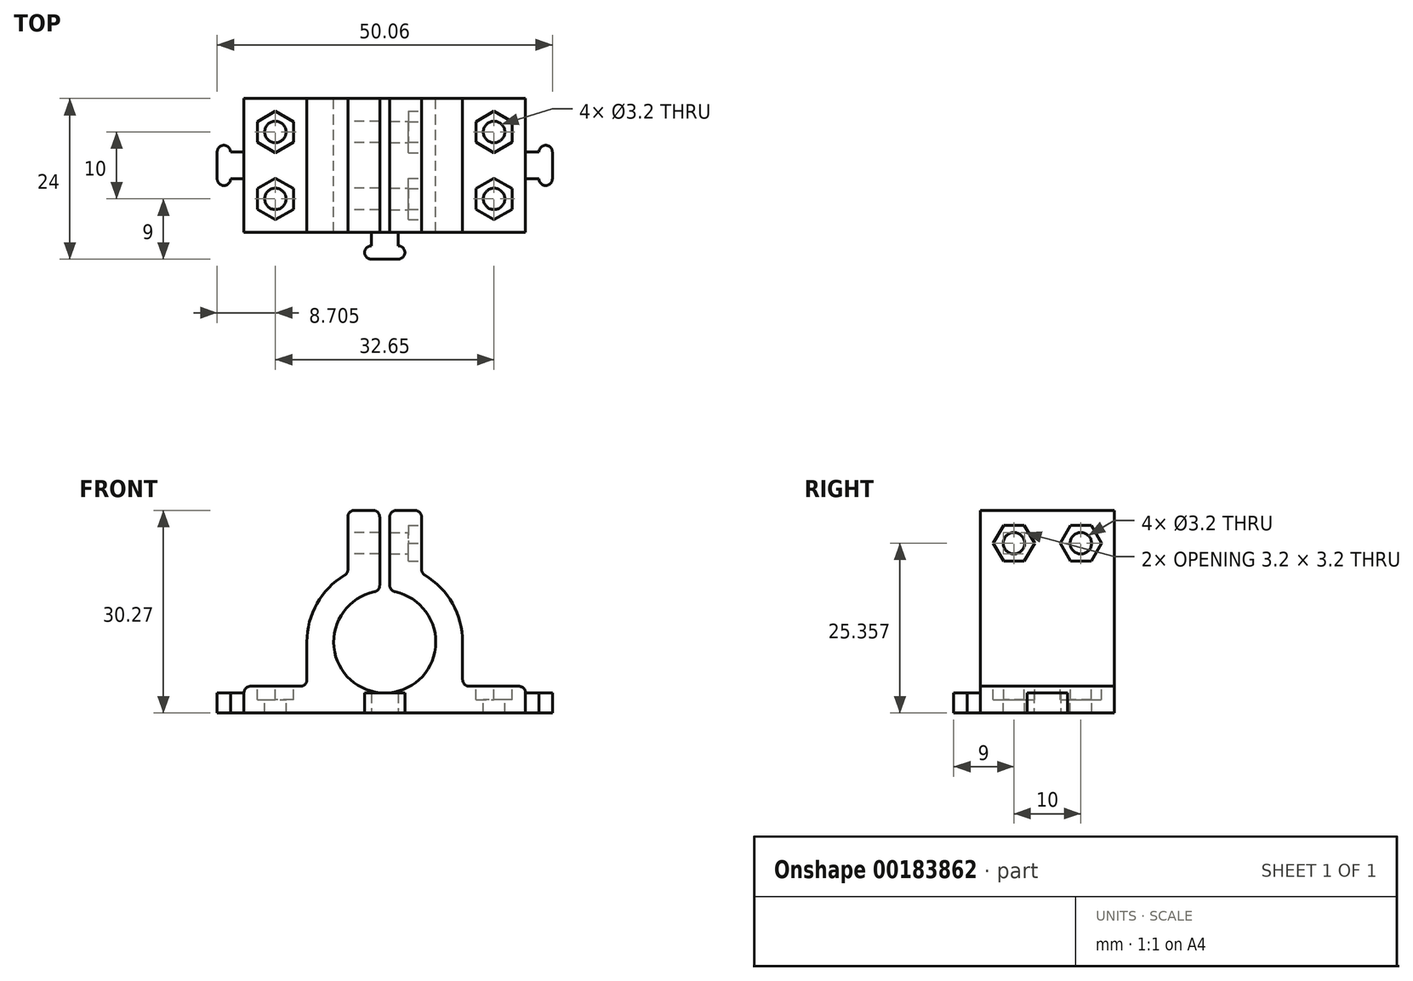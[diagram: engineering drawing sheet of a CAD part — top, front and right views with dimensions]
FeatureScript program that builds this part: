
annotation { "Feature Type Name" : "Feature", "Feature Type Description" : "" }
export const myFeature = defineFeature(function(context is Context, id is Id, definition is map)
    precondition{}
    {
        {
            assignVariable(context, id + "F0", {"name" : "hole_d_ideal", "anyValue" : 3});
        }
        {
            assignVariable(context, id + "F1", {"name" : "hole_d_pad", "anyValue" : 0.2});
        }
        {
            assignVariable(context, id + "F2", {"name" : "nut_h", "anyValue" : 2});
        }
        {
            assignVariable(context, id + "F3", {"name" : "hole_d", "anyValue" : getVariable(context, 'hole_d_ideal') + getVariable(context, 'hole_d_pad')});
        }
        {
            assignVariable(context, id + "F4", {"name" : "bear_l", "anyValue" : 24});
        }
        {
            assignVariable(context, id + "F5", {"name" : "base_l", "anyValue" : getVariable(context, 'bear_l') - 4});
        }
        {
            var Q0;
            Q0=qCreatedBy(makeId("Front.planeOp"),FACE);
            var sketch = newSketch(context, id + "F6", { "sketchPlane" : qUnion([Q0])});
            skLineSegment(sketch, "E0", {"start": v(0, 0) * mm, "end": v(21.03, 0) * mm});
            skLineSegment(sketch, "E1", {"start": v(21.03, 0) * mm, "end": v(21.03, 4) * mm});
            skLineSegment(sketch, "E2", {"start": v(21.03, 4) * mm, "end": v(11.62, 4) * mm});
            skLineSegment(sketch, "E3", {"start": v(11.62, 4) * mm, "end": v(11.62, 10.62) * mm});
            skArc(sketch, "E4", {"start": v(0, 3) * mm, "mid": v(7.62, 10.25) * mm, "end": v(0.75, 18.21) * mm});
            skLineSegment(sketch, "E5.top", {"start": v(0.75, 30.27) * mm, "end": v(5.5, 30.27) * mm});
            skLineSegment(sketch, "E5.right", {"start": v(5.5, 20.87) * mm, "end": v(5.5, 30.27) * mm});
            skLineSegment(sketch, "E6.trimOffspring", {"start": v(0, 3) * mm, "end": v(0, 0) * mm});
            skPoint(sketch, "E7", {"position": v(11.62, 10.62) * mm});
            skArc(sketch, "E8", {"start": v(11.62, 10.62) * mm, "mid": v(9.98, 16.6) * mm, "end": v(5.5, 20.87) * mm});
            skLineSegment(sketch, "E9", {"start": v(0.75, 18.21) * mm, "end": v(0.75, 30.27) * mm});
            skSolve(sketch);
        }
        {
            var Q0;
            Q0 = qSketchRegion(id + "F6", true);
            extrude(context, id + "F7", {"entities" : qUnion([Q0]), "endBound" : BoundingType.SYMMETRIC, "depth" : (getVariable(context, 'base_l')) * mm});
        }
        {
            var Q0;
            Q0=makeQuery(id+"F7.opExtrude","SWEPT_EDGE",EDGE,{"disambiguationData":[OSD([sQuery(id+"F6.wireOp",EDGE,"E4"),sQuery(id+"F6.wireOp",EDGE,"E9")])]});
            var Q1;
            Q1=makeQuery(id+"F7.opExtrude","SWEPT_EDGE",EDGE,{"disambiguationData":[OSD([sQuery(id+"F6.wireOp",EDGE,"E5.top"),sQuery(id+"F6.wireOp",EDGE,"E5.right")])]});
            var Q2;
            Q2=makeQuery(id+"F7.opExtrude","SWEPT_EDGE",EDGE,{"disambiguationData":[OSD([sQuery(id+"F6.wireOp",EDGE,"E5.top"),sQuery(id+"F6.wireOp",EDGE,"E5.right")])]});
            var Q3;
            Q3=makeQuery(id+"F7.opExtrude","SWEPT_EDGE",EDGE,{"disambiguationData":[OSD([sQuery(id+"F6.wireOp",EDGE,"E5.right"),sQuery(id+"F6.wireOp",EDGE,"E8")])]});
            var Q4;
            Q4=makeQuery(id+"F7.opExtrude","SWEPT_EDGE",EDGE,{"disambiguationData":[OSD([sQuery(id+"F6.wireOp",EDGE,"E2"),sQuery(id+"F6.wireOp",EDGE,"E3")])]});
            var Q5;
            Q5=makeQuery(id+"F7.opExtrude","SWEPT_EDGE",EDGE,{"disambiguationData":[OSD([sQuery(id+"F6.wireOp",EDGE,"E3"),sQuery(id+"F6.wireOp",EDGE,"E8")])]});
            var Q6;
            Q6=makeQuery(id+"F7.opExtrude","SWEPT_EDGE",EDGE,{"disambiguationData":[OSD([sQuery(id+"F6.wireOp",EDGE,"E2"),sQuery(id+"F6.wireOp",EDGE,"E3")])]});
            var Q7;
            Q7=makeQuery(id+"F7.opExtrude","SWEPT_EDGE",EDGE,{"disambiguationData":[OSD([sQuery(id+"F6.wireOp",EDGE,"E1"),sQuery(id+"F6.wireOp",EDGE,"E2")])]});
            var Q8;
            Q8=makeQuery(id+"F7.opExtrude","SWEPT_EDGE",EDGE,{"disambiguationData":[OSD([sQuery(id+"F6.wireOp",EDGE,"E5.top"),sQuery(id+"F6.wireOp",EDGE,"E9")])]});
            var Q9;
            Q9=makeQuery(id+"F7.opExtrude","SWEPT_EDGE",EDGE,{"disambiguationData":[OSD([sQuery(id+"F6.wireOp",EDGE,"E5.top"),sQuery(id+"F6.wireOp",EDGE,"E5.right")])]});
            fillet(context, id + "F8", {"entities" : qUnion([Q0, Q1, Q2, Q3, Q4, Q5, Q6, Q7, Q8, Q9]), "radius" : 1 * mm, "tangentPropagation" : true, "allowEdgeOverflow" : false});
        }
        {
            var Q0;
            Q0=makeQuery(id+"F7.opExtrude","SWEPT_FACE",FACE,{"disambiguationData":[OSD([sQuery(id+"F6.wireOp",EDGE,"E5.right")])]});
            var sketch = newSketch(context, id + "F9", { "sketchPlane" : qUnion([Q0])});
            skLineSegment(sketch, "E10", {"start": v(-10, 25.36) * mm, "end": v(0, 25.36) * mm, "construction": true});
            skLineSegment(sketch, "E11", {"start": v(0, 25.36) * mm, "end": v(10, 25.36) * mm, "construction": true});
            skPoint(sketch, "E12", {"position": v(-5, 25.36) * mm});
            skPoint(sketch, "E13", {"position": v(5, 25.36) * mm});
            skPoint(sketch, "E14", {"position": v(-10, 25.36) * mm});
            skCircle(sketch, "E15.cCircle", {"center": v(-5, 25.36) * mm, "radius": 3.1 * mm, "construction": true});
            skLineSegment(sketch, "E15.0", {"start": v(-3.45, 28.04) * mm, "end": v(-1.9, 25.36) * mm});
            skLineSegment(sketch, "E15.1", {"start": v(-1.9, 25.36) * mm, "end": v(-3.45, 22.67) * mm});
            skLineSegment(sketch, "E15.2", {"start": v(-3.45, 22.67) * mm, "end": v(-6.55, 22.67) * mm});
            skLineSegment(sketch, "E15.3", {"start": v(-6.55, 22.67) * mm, "end": v(-8.1, 25.36) * mm});
            skLineSegment(sketch, "E15.4", {"start": v(-8.1, 25.36) * mm, "end": v(-6.55, 28.04) * mm});
            skLineSegment(sketch, "E15.5", {"start": v(-6.55, 28.04) * mm, "end": v(-3.45, 28.04) * mm});
            skCircle(sketch, "E16.cCircle", {"center": v(5, 25.36) * mm, "radius": 3.1 * mm, "construction": true});
            skLineSegment(sketch, "E16.0", {"start": v(3.45, 28.04) * mm, "end": v(6.55, 28.04) * mm});
            skLineSegment(sketch, "E16.1", {"start": v(6.55, 28.04) * mm, "end": v(8.1, 25.36) * mm});
            skLineSegment(sketch, "E16.2", {"start": v(8.1, 25.36) * mm, "end": v(6.55, 22.67) * mm});
            skLineSegment(sketch, "E16.3", {"start": v(6.55, 22.67) * mm, "end": v(3.45, 22.67) * mm});
            skLineSegment(sketch, "E16.4", {"start": v(3.45, 22.67) * mm, "end": v(1.9, 25.36) * mm});
            skLineSegment(sketch, "E16.5", {"start": v(1.9, 25.36) * mm, "end": v(3.45, 28.04) * mm});
            skSolve(sketch);
        }
        {
            var Q0;
            Q0=sQuery(id+"F9.wireOp",VERTEX,"E12");
            var Q1;
            Q1=sQuery(id+"F9.wireOp",VERTEX,"E13");
            var Q2;
            Q2=makeQuery(id+"F7.opExtrude","SWEPT_BODY",BODY,{"disambiguationData":[OSD([sQuery(id+"F6.wireOp",EDGE,"E0"),sQuery(id+"F6.wireOp",EDGE,"E1"),sQuery(id+"F6.wireOp",EDGE,"E2"),sQuery(id+"F6.wireOp",EDGE,"E3"),sQuery(id+"F6.wireOp",EDGE,"HN3FgCps-Q0FI-6wMn-lYnE-is20jSelRbzD"),sQuery(id+"F6.wireOp",EDGE,"b23bd27e-2929-432b-ba1c-64cbd251a3970.MirrorCS"),sQuery(id+"F6.wireOp",EDGE,"2befd7d9-4525-4836-902e-ac56c651b7a10.MirrorCS"),sQuery(id+"F6.wireOp",EDGE,"45559492-88bf-4efa-95f0-e6e5f18770240.MirrorCS"),sQuery(id+"F6.wireOp",EDGE,"8ad17469-4e6f-47e4-abdb-9c6c75d0893b0.MirrorCS"),sQuery(id+"F6.wireOp",EDGE,"a78b3f0d-bb6c-460a-9a47-5c75e2336ab60.MirrorCS"),sQuery(id+"F6.wireOp",EDGE,"E4"),sQuery(id+"F6.wireOp",EDGE,"E5.top"),sQuery(id+"F6.wireOp",EDGE,"E5.right"),sQuery(id+"F6.wireOp",EDGE,"feef7f43-0b31-40ae-9d8b-5ec27f5b37380.MirrorCS"),sQuery(id+"F6.wireOp",EDGE,"c6b9ee4f-cf07-424e-834d-23f5c7f768820.MirrorCS")])]});
            hole(context, id + "F10", {"style" : HoleStyle.SIMPLE, "endStyle" : HoleEndStyle.THROUGH, "holeDiameter" : (getVariable(context, 'hole_d')) * mm, "locations" : qUnion([Q0, Q1]), "scope" : qUnion([Q2]), "isTappedThrough" : true});
        }
        {
            var Q0;
            Q0=makeQuery(id+"F7.opExtrude","SWEPT_FACE",FACE,{"disambiguationData":[OSD([sQuery(id+"F6.wireOp",EDGE,"E2")])]});
            var sketch = newSketch(context, id + "F11", { "sketchPlane" : qUnion([Q0])});
            skLineSegment(sketch, "E17", {"start": v(16.32, 10) * mm, "end": v(16.32, 0) * mm, "construction": true});
            skLineSegment(sketch, "E18", {"start": v(16.32, 0) * mm, "end": v(16.32, -10) * mm, "construction": true});
            skPoint(sketch, "E19", {"position": v(16.32, 5) * mm});
            skPoint(sketch, "E20", {"position": v(16.32, -5) * mm});
            skCircle(sketch, "E21.cCircle", {"center": v(16.32, 5) * mm, "radius": 3.1 * mm, "construction": true});
            skLineSegment(sketch, "E21.0", {"start": v(13.64, 6.55) * mm, "end": v(16.33, 8.1) * mm});
            skLineSegment(sketch, "E21.1", {"start": v(16.33, 8.1) * mm, "end": v(19, 6.55) * mm});
            skLineSegment(sketch, "E21.2", {"start": v(19, 6.55) * mm, "end": v(19, 3.45) * mm});
            skLineSegment(sketch, "E21.3", {"start": v(19, 3.45) * mm, "end": v(16.33, 1.9) * mm});
            skLineSegment(sketch, "E21.4", {"start": v(16.33, 1.9) * mm, "end": v(13.64, 3.45) * mm});
            skLineSegment(sketch, "E21.5", {"start": v(13.64, 3.45) * mm, "end": v(13.64, 6.55) * mm});
            skCircle(sketch, "E22.cCircle", {"center": v(16.32, -5) * mm, "radius": 3.1 * mm, "construction": true});
            skLineSegment(sketch, "E22.0", {"start": v(13.64, -3.45) * mm, "end": v(16.33, -1.9) * mm});
            skLineSegment(sketch, "E22.1", {"start": v(16.33, -1.9) * mm, "end": v(19, -3.45) * mm});
            skLineSegment(sketch, "E22.2", {"start": v(19, -3.45) * mm, "end": v(19, -6.55) * mm});
            skLineSegment(sketch, "E22.3", {"start": v(19, -6.55) * mm, "end": v(16.33, -8.1) * mm});
            skLineSegment(sketch, "E22.4", {"start": v(16.33, -8.1) * mm, "end": v(13.64, -6.55) * mm});
            skLineSegment(sketch, "E22.5", {"start": v(13.64, -6.55) * mm, "end": v(13.64, -3.45) * mm});
            skSolve(sketch);
        }
        {
            var Q0;
            Q0=sQuery(id+"F11.wireOp",VERTEX,"E19");
            var Q1;
            Q1=sQuery(id+"F11.wireOp",VERTEX,"E20");
            var Q2;
            Q2=makeQuery(id+"F7.opExtrude","SWEPT_BODY",BODY,{"disambiguationData":[OSD([sQuery(id+"F6.wireOp",EDGE,"E0"),sQuery(id+"F6.wireOp",EDGE,"E1"),sQuery(id+"F6.wireOp",EDGE,"E2"),sQuery(id+"F6.wireOp",EDGE,"E3"),sQuery(id+"F6.wireOp",EDGE,"HN3FgCps-Q0FI-6wMn-lYnE-is20jSelRbzD"),sQuery(id+"F6.wireOp",EDGE,"b23bd27e-2929-432b-ba1c-64cbd251a3970.MirrorCS"),sQuery(id+"F6.wireOp",EDGE,"2befd7d9-4525-4836-902e-ac56c651b7a10.MirrorCS"),sQuery(id+"F6.wireOp",EDGE,"45559492-88bf-4efa-95f0-e6e5f18770240.MirrorCS"),sQuery(id+"F6.wireOp",EDGE,"8ad17469-4e6f-47e4-abdb-9c6c75d0893b0.MirrorCS"),sQuery(id+"F6.wireOp",EDGE,"a78b3f0d-bb6c-460a-9a47-5c75e2336ab60.MirrorCS")])]});
            hole(context, id + "F12", {"style" : HoleStyle.SIMPLE, "endStyle" : HoleEndStyle.THROUGH, "holeDiameter" : (getVariable(context, 'hole_d')) * mm, "locations" : qUnion([Q0, Q1]), "scope" : qUnion([Q2]), "isTappedThrough" : true});
        }
        {
            var Q0;
            Q0=makeQuery(id+"F11.imprint","IMPRINT",FACE,{"disambiguationData":[TD([[makeQuery(id+"F11.imprint","IMPRINT",EDGE,{"derivedFrom":sQuery(id+"F11.wireOp",EDGE,"E21.0")}),-1.0]])]});
            var Q1;
            Q1=makeQuery(id+"F11.imprint","IMPRINT",FACE,{"disambiguationData":[TD([[makeQuery(id+"F11.imprint","IMPRINT",EDGE,{"derivedFrom":sQuery(id+"F11.wireOp",EDGE,"E22.0")}),-1.0]])]});
            extrude(context, id + "F13", {"entities" : qUnion([Q0, Q1]), "operationType" : NewBodyOperationType.REMOVE, "oppositeDirection" : true, "depth" : (getVariable(context, 'nut_h')) * mm});
        }
        {
            var Q0;
            Q0=makeQuery(id+"F7.opExtrude","SWEPT_FACE",FACE,{"disambiguationData":[OSD([sQuery(id+"F6.wireOp",EDGE,"E0")])]});
            var sketch = newSketch(context, id + "F14", { "sketchPlane" : qUnion([Q0])});
            skLineSegment(sketch, "E23", {"start": v(0, 10) * mm, "end": v(0, 14) * mm});
            skLineSegment(sketch, "E24", {"start": v(0, 14) * mm, "end": v(2, 14) * mm});
            skArc(sketch, "E25", {"start": v(2, 14) * mm, "mid": v(3, 13) * mm, "end": v(2, 12) * mm});
            skLineSegment(sketch, "E26", {"start": v(2, 12) * mm, "end": v(2, 10) * mm});
            skLineSegment(sketch, "E27", {"start": v(0, 10) * mm, "end": v(2, 10) * mm});
            skLineSegment(sketch, "E28", {"start": v(21.03, 0) * mm, "end": v(25.03, 0) * mm});
            skLineSegment(sketch, "E29", {"start": v(25.03, 0) * mm, "end": v(25.03, -2) * mm});
            skArc(sketch, "E30", {"start": v(25.03, -2) * mm, "mid": v(24.03, -3) * mm, "end": v(23.02, -2) * mm});
            skLineSegment(sketch, "E31", {"start": v(23.02, -2) * mm, "end": v(21.03, -2) * mm});
            skLineSegment(sketch, "E32", {"start": v(21.03, 0) * mm, "end": v(21.03, -2) * mm});
            skLineSegment(sketch, "E33.MirrorCS", {"start": v(23.02, 2) * mm, "end": v(21.03, 2) * mm});
            skLineSegment(sketch, "E34.MirrorCS", {"start": v(21.03, 0) * mm, "end": v(21.03, 2) * mm});
            skArc(sketch, "E35.MirrorCS", {"start": v(25.03, 2) * mm, "mid": v(24.03, 3) * mm, "end": v(23.02, 2) * mm});
            skLineSegment(sketch, "E36.MirrorCS", {"start": v(25.03, 0) * mm, "end": v(25.03, 2) * mm});
            skSolve(sketch);
        }
        {
            var Q0;
            Q0 = qSketchRegion(id + "F14", true);
            extrude(context, id + "F15", {"entities" : qUnion([Q0]), "operationType" : NewBodyOperationType.ADD, "oppositeDirection" : true, "depth" : 3 * mm});
        }
        {
            var Q0;
            Q0=makeQuery(id+"F7.opExtrude","SWEPT_BODY",BODY,{"disambiguationData":[OSD([sQuery(id+"F6.wireOp",EDGE,"E0"),sQuery(id+"F6.wireOp",EDGE,"E1"),sQuery(id+"F6.wireOp",EDGE,"E2"),sQuery(id+"F6.wireOp",EDGE,"E3"),sQuery(id+"F6.wireOp",EDGE,"E4"),sQuery(id+"F6.wireOp",EDGE,"E5.top"),sQuery(id+"F6.wireOp",EDGE,"E5.right"),sQuery(id+"F6.wireOp",EDGE,"E6.trimOffspring"),sQuery(id+"F6.wireOp",EDGE,"E8"),sQuery(id+"F6.wireOp",EDGE,"E9")])]});
            var Q1;
            Q1=qCreatedBy(makeId("Right.planeOp"),FACE);
            mirror(context, id + "F16", {"operationType" : NewBodyOperationType.ADD, "entities" : qUnion([Q0]), "mirrorPlane" : qUnion([Q1])});
        }
        {
            var Q0;
            Q0=makeQuery(id+"F9.imprint","IMPRINT",FACE,{"disambiguationData":[TD([[makeQuery(id+"F9.imprint","IMPRINT",EDGE,{"derivedFrom":sQuery(id+"F9.wireOp",EDGE,"E15.0")}),-1.0]])]});
            var Q1;
            Q1=makeQuery(id+"F9.imprint","IMPRINT",FACE,{"disambiguationData":[TD([[makeQuery(id+"F9.imprint","IMPRINT",EDGE,{"derivedFrom":sQuery(id+"F9.wireOp",EDGE,"E16.0")}),-1.0]])]});
            extrude(context, id + "F17", {"entities" : qUnion([Q0, Q1]), "operationType" : NewBodyOperationType.REMOVE, "oppositeDirection" : true, "depth" : (getVariable(context, 'nut_h')) * mm});
        }
    });
